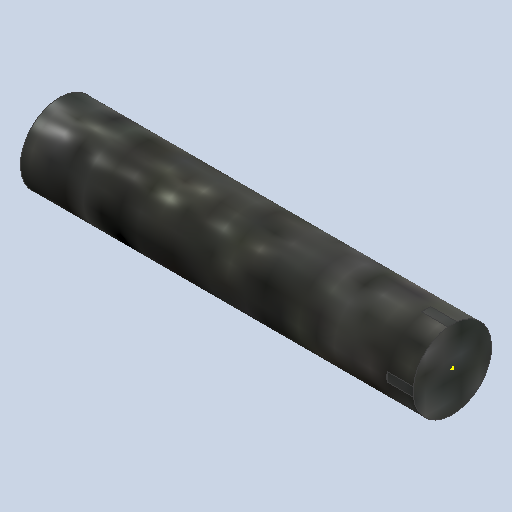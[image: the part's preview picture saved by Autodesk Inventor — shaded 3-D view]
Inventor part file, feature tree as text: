
AUTODESK INVENTOR PART (.ipt)
format: ipt  version: 2024.3 (Build 283343000, 343)  size: 245,248 bytes
history: native  units: mm
features: sketch x4, extrude x3, projected_geometry x1
ambient origin geometry x8: Origin, YZ Plane, XZ Plane, XY Plane, X Axis, Y Axis, Z Axis, Center Point
bodies: Solid1 (feature_tree)
feature tree (8):
  extrude  "Extrusion1"  Depth=15.0mm TaperAngle=0.0deg
  extrude  "Extrusion2"  Depth=1.0mm TaperAngle=0.0deg
  sketch  "Sketch3"  dims[d6=1.49mm d7=1.0mm d8=0.0mm]
  extrude  "Extrusion3"  Depth=1.0mm TaperAngle=0.0deg
  sketch  "Sketch1"  dims[d0=3.0mm d1=15.0mm d2=0.0mm]
  sketch  "Sketch2"  dims[d3=1.49mm d4=1.0mm d5=0.0mm]
  projected_geometry  "Projected Loop1"
  sketch  "Sketch4"
